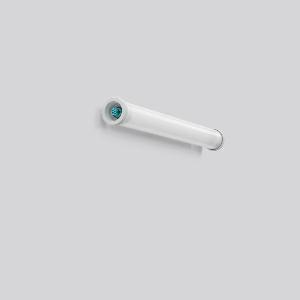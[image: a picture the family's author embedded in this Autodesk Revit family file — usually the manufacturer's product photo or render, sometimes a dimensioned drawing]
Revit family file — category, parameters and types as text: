
# Revit family: planox_tube_601070_002_1_76_ad33
name_source: partatom
category: Lighting Fixtures
units: mm (PartAtom-declared; Revit-internal decimal feet)

## family parameters
Cut with Voids When Loaded = No
Host = Face
Light Source = No
Part Type = Normal
Room Calculation Point = No
Round Connector Dimension = Use Diameter
Shared = No

## types (1)
- PLANOX TUBE (1 x LED Modul 840, 3500 lm, 4000)
    Apparent Load = 31 VA
    Approval mark = CE
    CIE Flux Codes = 41 70 89 89 100
    Color Rendering = 80
    Color Temperature = 4000
    Default Elevation = 1800 mm
    Description = Series: PLANOX TUBE
Robust protective tube luminaire for tough requirements. Rack made of sheet steel, white powder coated. End caps made of plastic (polyamide) grey. Diffuser made of plastic (polycarbonate), opal, shockproof. Symmetrical light distribution. Homogeneous light distribution. With accessories for wall, ceiling or pendant mounting. Driver integrated. Easy installation with the Plug+Play Wieland RST CLASSIC plug-in system. Luminaire with integrated through-wiring for series connection of further luminaires by two Wieland RST Classic plug connectors (plug and socket). Accessories for electrical connection must be ordered separately. Mounting set must be ordered separately. Luminaire with limited surface temperature in accordance with EN 60598-2-24 for use in environments in which a deposit of conductive dust on the luminaire can be expected. Qualified for use in the food and drink industry. Suitable for lighting in public car parks and public off-street parking spaces according to DIN 67528. Environmentally friendly and resource-saving due to replaceable components. 
Colour: white
Diameter: 78 mm
Length: 722 mm
Lamp: LED
Socket: without socket
Colour temperature: 4000K
Colour rendering index (CRI): 83
System power: 31 W
Rated luminous flux: 3500 lm
Beam angle Down: 139° / 106°
Luminous efficiency: 113 lm/W
Control gear: Converter, dimmable, DALI
Protection class: I
Type of protection: IP 67
    Height = 0 mm  [stored 0 ft]
    Lamp = 1 x LED Modul 840
    Lamp Light Flux = 3500 lm
    Lamp count = 1
    Length = 722 mm
    Lifetime = 50000 h
    Luminous efficacy = 113 lm/W
    Manufacturer = RZB
    ModVariant = No
    Model = 601070.002.1.76
    Mounting Place = Ceiling, Wall
    Mounting Type = Surface mounted
    Number of Poles = 1
    OnlyDefault = Yes
    Power Factor = 1
    Product Name = PLANOX TUBE
    Product group = Surface mounted luminaires for moist/humid enviroments
    ProductGroupID = 308
    Protection Class = Protection class I
    Protection Degree = IP 67
    RLX_Detail_Level = 1
    RLX_Emergency_Light_Flux = 0 lm
    RLX_Emergency_Type = 0
    RLX_Emergency_Type_DB = No
    RlxData = <blob elided: 31845 chars, md5=a49138b4>
    Socket = socket
    Standby Power = 0 W
    System Light Flux = 3500 lm
    System Power = 31 W
    Type Comments = Product without accessories
    Type Image = 601070.002.76.jpg
    URL = http://relux.com
    VarID = ---
    Voltage = 230 V
    Voltage Range = 220-240 V
    Weight = 0.00 kg
    Width = 0 mm  [stored 0 ft]

note: [stored X ft] marks values corroborated as IEEE doubles in the binary element streams (Revit-internal decimal feet)

## geometry (parser evidence)
native form markers: Blend x4, Sweep x15
no freeform markers — native parametric forms only
